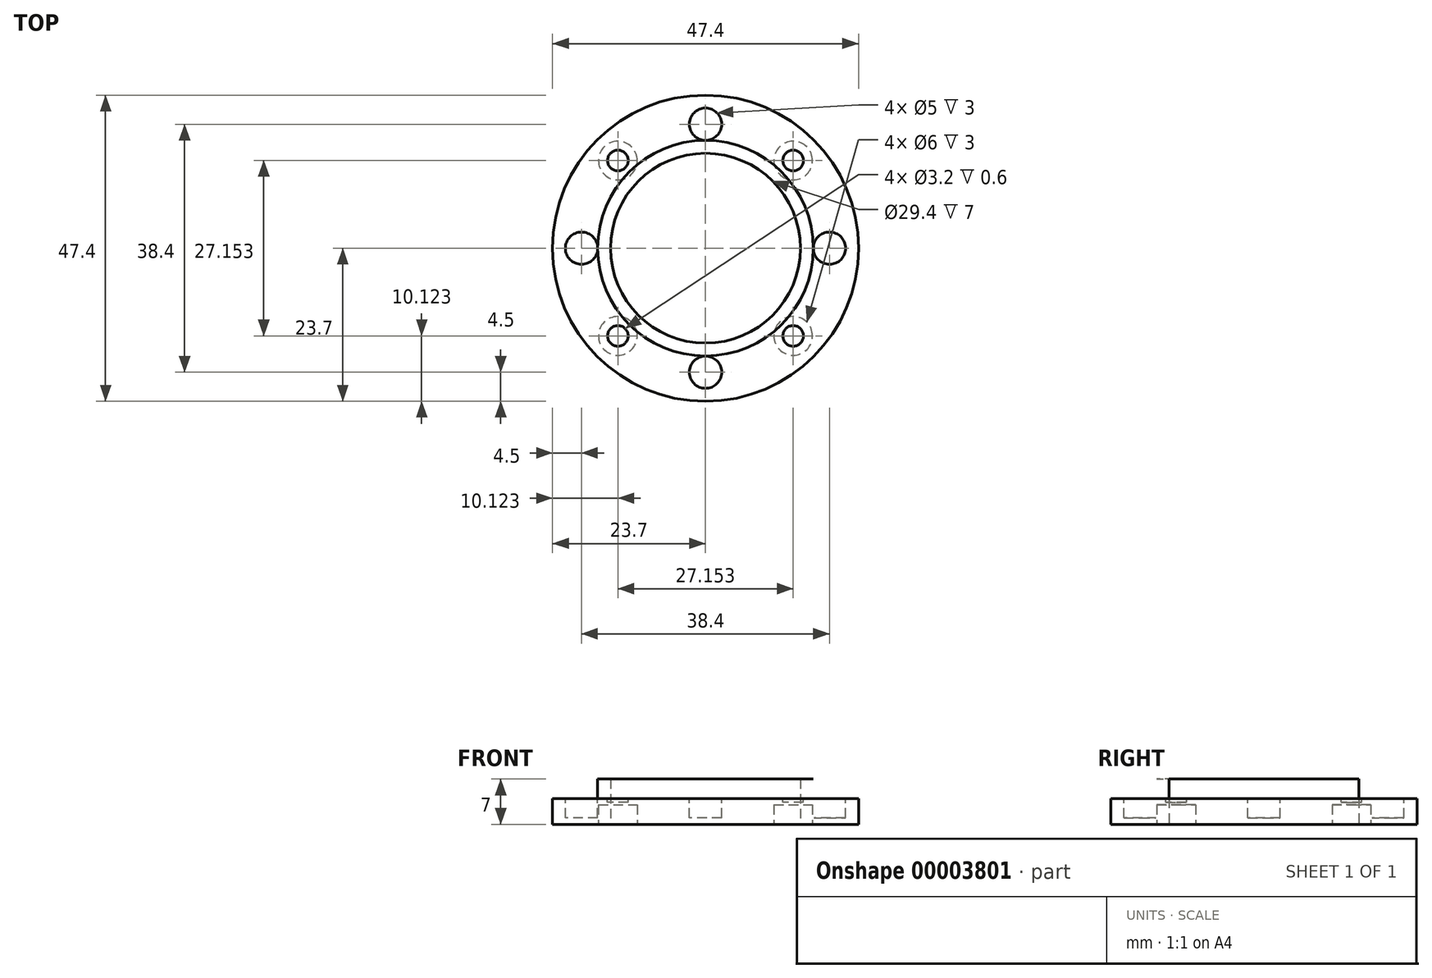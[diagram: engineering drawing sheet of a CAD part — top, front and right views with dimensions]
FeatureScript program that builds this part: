
annotation { "Feature Type Name" : "Feature", "Feature Type Description" : "" }
export const myFeature = defineFeature(function(context is Context, id is Id, definition is map)
    precondition{}
    {
        {
            var Q0;
            Q0=qCreatedBy(makeId("Top.planeOp"),FACE);
            var sketch = newSketch(context, id + "F0", { "sketchPlane" : qUnion([Q0])});
            skCircle(sketch, "E0", {"center": v(0, 0) * mm, "radius": 23.7 * mm});
            skCircle(sketch, "E1", {"center": v(0, 0) * mm, "radius": 14.7 * mm});
            skSolve(sketch);
        }
        {
            var Q0;
            Q0=makeQuery(id+"F0.imprint","IMPRINT",FACE,{"disambiguationData":[TD([[makeQuery(id+"F0.imprint","IMPRINT",EDGE,{"derivedFrom":sQuery(id+"F0.wireOp",EDGE,"E0")}),1.0]])]});
            extrude(context, id + "F1", {"entities" : qUnion([Q0]), "depth" : 3 * mm});
        }
        {
            var Q0;
            Q0=makeQuery(id+"F1.opExtrude","CAP_FACE",FACE,{"disambiguationData":[OSD([sQuery(id+"F0.wireOp",EDGE,"E0"),sQuery(id+"F0.wireOp",EDGE,"990f527f-03d4-477e-94be-eea046fbdff1"),sQuery(id+"F0.wireOp",EDGE,"55a7449c-1202-42ac-ae43-5e7a6f932236.1.1"),sQuery(id+"F0.wireOp",EDGE,"55a7449c-1202-42ac-ae43-5e7a6f932236.2.1"),sQuery(id+"F0.wireOp",EDGE,"55a7449c-1202-42ac-ae43-5e7a6f932236.3.1")])],"isStart":false});
            var sketch = newSketch(context, id + "F2", { "sketchPlane" : qUnion([Q0])});
            skCircle(sketch, "E2.0", {"center": v(0, 0) * mm, "radius": 23.7 * mm});
            skPoint(sketch, "E2.9", {"position": v(0, 0) * mm});
            skCircle(sketch, "E3", {"center": v(0, 19.2) * mm, "radius": 2.5 * mm});
            skCircle(sketch, "E4.1.0", {"center": v(-19.2, 0) * mm, "radius": 2.5 * mm});
            skCircle(sketch, "E4.2.0", {"center": v(0, -19.2) * mm, "radius": 2.5 * mm});
            skCircle(sketch, "E4.3.0", {"center": v(19.2, 0) * mm, "radius": 2.5 * mm});
            skSolve(sketch);
        }
        {
            var Q0;
            Q0=makeQuery(id+"F2.imprint","IMPRINT",FACE,{"disambiguationData":[TD([[makeQuery(id+"F2.imprint","IMPRINT",EDGE,{"derivedFrom":sQuery(id+"F2.wireOp",EDGE,"E4.1.0")}),1.0]])]});
            var Q1;
            Q1=makeQuery(id+"F2.imprint","IMPRINT",FACE,{"disambiguationData":[TD([[makeQuery(id+"F2.imprint","IMPRINT",EDGE,{"derivedFrom":sQuery(id+"F2.wireOp",EDGE,"E3")}),1.0]])]});
            var Q2;
            Q2=makeQuery(id+"F2.imprint","IMPRINT",FACE,{"disambiguationData":[TD([[makeQuery(id+"F2.imprint","IMPRINT",EDGE,{"derivedFrom":sQuery(id+"F2.wireOp",EDGE,"E4.3.0")}),1.0]])]});
            var Q3;
            Q3=makeQuery(id+"F2.imprint","IMPRINT",FACE,{"disambiguationData":[TD([[makeQuery(id+"F2.imprint","IMPRINT",EDGE,{"derivedFrom":sQuery(id+"F2.wireOp",EDGE,"E4.2.0")}),1.0]])]});
            extrude(context, id + "F3", {"entities" : qUnion([Q0, Q1, Q2, Q3]), "operationType" : NewBodyOperationType.REMOVE, "oppositeDirection" : true, "depth" : 2 * mm});
        }
        {
            var Q0;
            Q0=makeQuery(id+"F1.opExtrude","CAP_FACE",FACE,{"disambiguationData":[OSD([sQuery(id+"F0.wireOp",EDGE,"E0"),sQuery(id+"F0.wireOp",EDGE,"E1")])],"isStart":false});
            var sketch = newSketch(context, id + "F4", { "sketchPlane" : qUnion([Q0])});
            skCircle(sketch, "E5.0", {"center": v(0, 0) * mm, "radius": 14.7 * mm});
            skSolve(sketch);
        }
        {
            var Q0;
            Q0=makeQuery(id+"F4.imprint","IMPRINT",FACE,{"disambiguationData":[TD([[makeQuery(id+"F4.imprint","IMPRINT",EDGE,{"derivedFrom":sQuery(id+"F4.wireOp",EDGE,"E5.0")}),-1.0]])]});
            var Q1;
            Q1=makeQuery(id+"F4.imprint","IMPRINT",FACE,{"disambiguationData":[TD([[makeQuery(id+"F4.imprint","IMPRINT",EDGE,{"derivedFrom":makeQuery(id+"F3.boolean.opBoolean","COPY",EDGE,{"derivedFrom":makeQuery(id+"F3.opExtrude","CAP_EDGE",EDGE,{"disambiguationData":[OSD([sQuery(id+"F2.wireOp",EDGE,"E4.1.0")])],"isStart":true})})}),1.0]])]});
            var Q2;
            Q2=makeQuery(id+"F4.imprint","IMPRINT",FACE,{"disambiguationData":[TD([[makeQuery(id+"F4.imprint","IMPRINT",EDGE,{"derivedFrom":makeQuery(id+"F3.boolean.opBoolean","COPY",EDGE,{"derivedFrom":makeQuery(id+"F3.opExtrude","CAP_EDGE",EDGE,{"disambiguationData":[OSD([sQuery(id+"F2.wireOp",EDGE,"E3")])],"isStart":true})})}),1.0]])]});
            var Q3;
            Q3=makeQuery(id+"F4.imprint","IMPRINT",FACE,{"disambiguationData":[TD([[makeQuery(id+"F4.imprint","IMPRINT",EDGE,{"derivedFrom":makeQuery(id+"F3.boolean.opBoolean","COPY",EDGE,{"derivedFrom":makeQuery(id+"F3.opExtrude","CAP_EDGE",EDGE,{"disambiguationData":[OSD([sQuery(id+"F2.wireOp",EDGE,"E4.3.0")])],"isStart":true})})}),1.0]])]});
            var Q4;
            Q4=makeQuery(id+"F4.imprint","IMPRINT",FACE,{"disambiguationData":[TD([[makeQuery(id+"F4.imprint","IMPRINT",EDGE,{"derivedFrom":makeQuery(id+"F3.boolean.opBoolean","COPY",EDGE,{"derivedFrom":makeQuery(id+"F3.opExtrude","CAP_EDGE",EDGE,{"disambiguationData":[OSD([sQuery(id+"F2.wireOp",EDGE,"E4.2.0")])],"isStart":true})})}),1.0]])]});
            extrude(context, id + "F5", {"entities" : qUnion([Q0, Q1, Q2, Q3, Q4]), "operationType" : NewBodyOperationType.ADD, "depth" : 1 * mm});
        }
        {
            var Q0;
            Q0=makeQuery(id+"F5.opExtrude","CAP_FACE",FACE,{"disambiguationData":[OSD([sQuery(id+"F0.wireOp",EDGE,"E0"),sQuery(id+"F4.wireOp",EDGE,"E5.0")])],"isStart":false});
            var sketch = newSketch(context, id + "F6", { "sketchPlane" : qUnion([Q0])});
            skCircle(sketch, "E6", {"center": v(0, 0) * mm, "radius": 16.7 * mm});
            skSolve(sketch);
        }
        {
            var Q0;
            Q0=makeQuery(id+"F6.imprint","IMPRINT",FACE,{"disambiguationData":[TD([[makeQuery(id+"F6.imprint","IMPRINT",EDGE,{"derivedFrom":sQuery(id+"F6.wireOp",EDGE,"E6")}),1.0]])]});
            extrude(context, id + "F7", {"entities" : qUnion([Q0]), "operationType" : NewBodyOperationType.ADD, "depth" : 3 * mm});
        }
        {
            var Q0;
            Q0=makeQuery(id+"F1.opExtrude","CAP_FACE",FACE,{"disambiguationData":[OSD([sQuery(id+"F0.wireOp",EDGE,"E0"),sQuery(id+"F0.wireOp",EDGE,"E1")])],"isStart":true});
            var sketch = newSketch(context, id + "F8", { "sketchPlane" : qUnion([Q0])});
            skLineSegment(sketch, "E7", {"start": v(0, 0) * mm, "end": v(-13.58, -13.58) * mm, "construction": true});
            skCircle(sketch, "E8", {"center": v(-13.58, -13.58) * mm, "radius": 3 * mm});
            skCircle(sketch, "E9.1.0", {"center": v(13.58, -13.58) * mm, "radius": 3 * mm});
            skCircle(sketch, "E9.2.0", {"center": v(13.58, 13.58) * mm, "radius": 3 * mm});
            skCircle(sketch, "E9.3.0", {"center": v(-13.58, 13.58) * mm, "radius": 3 * mm});
            skPoint(sketch, "E9.center", {"position": v(0, 0) * mm});
            skSolve(sketch);
        }
        {
            var Q0;
            Q0=makeQuery(id+"F8.imprint","IMPRINT",FACE,{"disambiguationData":[TD([[makeQuery(id+"F8.imprint","IMPRINT",EDGE,{"derivedFrom":sQuery(id+"F8.wireOp",EDGE,"E8")}),1.0]])]});
            var Q1;
            Q1=makeQuery(id+"F8.imprint","IMPRINT",FACE,{"disambiguationData":[TD([[makeQuery(id+"F8.imprint","IMPRINT",EDGE,{"derivedFrom":sQuery(id+"F8.wireOp",EDGE,"E9.3.0")}),1.0]])]});
            var Q2;
            Q2=makeQuery(id+"F8.imprint","IMPRINT",FACE,{"disambiguationData":[TD([[makeQuery(id+"F8.imprint","IMPRINT",EDGE,{"derivedFrom":sQuery(id+"F8.wireOp",EDGE,"E9.2.0")}),1.0]])]});
            var Q3;
            Q3=makeQuery(id+"F8.imprint","IMPRINT",FACE,{"disambiguationData":[TD([[makeQuery(id+"F8.imprint","IMPRINT",EDGE,{"derivedFrom":sQuery(id+"F8.wireOp",EDGE,"E9.1.0")}),1.0]])]});
            extrude(context, id + "F9", {"entities" : qUnion([Q0, Q1, Q2, Q3]), "operationType" : NewBodyOperationType.REMOVE, "oppositeDirection" : true, "depth" : 3 * mm});
        }
        {
            var Q0;
            Q0=makeQuery(id+"F5.opExtrude","CAP_FACE",FACE,{"disambiguationData":[OSD([sQuery(id+"F0.wireOp",EDGE,"E0"),sQuery(id+"F4.wireOp",EDGE,"E5.0")])],"isStart":false});
            var sketch = newSketch(context, id + "F10", { "sketchPlane" : qUnion([Q0])});
            skCircle(sketch, "E10", {"center": v(13.58, 13.58) * mm, "radius": 1.6 * mm});
            skCircle(sketch, "E11.1.0", {"center": v(-13.58, 13.58) * mm, "radius": 1.6 * mm});
            skCircle(sketch, "E11.2.0", {"center": v(-13.58, -13.58) * mm, "radius": 1.6 * mm});
            skCircle(sketch, "E11.3.0", {"center": v(13.58, -13.58) * mm, "radius": 1.6 * mm});
            skPoint(sketch, "E11.center", {"position": v(0, 0) * mm});
            skSolve(sketch);
        }
        {
            var Q0;
            Q0=makeQuery(id+"F10.imprint","IMPRINT",FACE,{"disambiguationData":[TD([[makeQuery(id+"F10.imprint","IMPRINT",EDGE,{"derivedFrom":sQuery(id+"F10.wireOp",EDGE,"E11.1.0")}),1.0]])]});
            var Q1;
            Q1=makeQuery(id+"F10.imprint","IMPRINT",FACE,{"disambiguationData":[TD([[makeQuery(id+"F10.imprint","IMPRINT",EDGE,{"derivedFrom":sQuery(id+"F10.wireOp",EDGE,"E10")}),1.0]])]});
            var Q2;
            Q2=makeQuery(id+"F10.imprint","IMPRINT",FACE,{"disambiguationData":[TD([[makeQuery(id+"F10.imprint","IMPRINT",EDGE,{"derivedFrom":sQuery(id+"F10.wireOp",EDGE,"E11.3.0")}),1.0]])]});
            var Q3;
            Q3=makeQuery(id+"F10.imprint","IMPRINT",FACE,{"disambiguationData":[TD([[makeQuery(id+"F10.imprint","IMPRINT",EDGE,{"derivedFrom":sQuery(id+"F10.wireOp",EDGE,"E11.2.0")}),1.0]])]});
            extrude(context, id + "F11", {"entities" : qUnion([Q0, Q1, Q2, Q3]), "operationType" : NewBodyOperationType.REMOVE, "oppositeDirection" : true, "depth" : 0.6 * mm});
        }
    });
